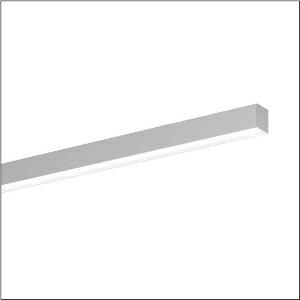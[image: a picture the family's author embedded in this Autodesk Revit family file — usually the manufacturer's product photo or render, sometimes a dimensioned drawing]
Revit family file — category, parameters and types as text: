
# Revit family: silica_r__21_51mx20da42sb_9e9a
name_source: partatom
category: Lighting Fixtures
units: mm (PartAtom-declared; Revit-internal decimal feet)

## family parameters
Cut with Voids When Loaded = No
Host = Face
Light Source = No
Part Type = Normal
Room Calculation Point = No
Round Connector Dimension = Use Diameter
Shared = No

## types (1)
- --- (1 x LED, 2400 lm, 15.2 W, 4000K)
    Apparent Load = 15 VA
    CIE Flux Codes = 48 79 96 100 100
    Color Rendering = 80
    Color Temperature = 4000K
    Default Elevation = 1800 mm
    Description = Silica® 21, office luminaire, primary optical cover: cover, of PMMA, opal, light emission: direct distribution, primary light characteristic: symmetric, installation type: surface-mounted, LED, rated luminous flux: 2.400lm, luminous efficacy: 158lm/W, light colour: 840, colour temperature: 4000K, with terminal, 3+2-pole, max. 2.5mm², mains connection: 220..240V, AC, 50/60Hz, rated input power: 15.2W, luminaire housing, of aluminium, metallic grey (RAL 9006), length: 1.204mm, width: 53mm, height: 53mm, protection rating (complete): IP20, insulation class (complete): insulation class I (protective earthing), certification: CE, permissible operating ambient temperature: 0..+35°C, standard: EN 50419, packaging unit: 1 piece
    Height = 0 mm  [stored 0 ft]
    Lamp = 1 x LED
    Lamp Light Flux = 2400 lm
    Lamp Power = 15.2 W
    Lamp count = 1
    Length = 1204 mm
    Luminous efficacy = 158 lm/W
    Manufacturer = Siteco
    ModVariant = No
    Model = 51MX20DA42SB
    Mounting Place = Ceiling
    Mounting Type = Recessed
    Number of Poles = 1
    OnlyDefault = Yes
    Power Factor = 1
    Product Name = Silica® 21
    Product group = office luminaire | ceiling recessed
    ProductGroupID = 401
    Protection Class = Protection class I
    Protection Degree = IP 20
    RLX_Detail_Level = 1
    RLX_Emergency_Light_Flux = 0 lm
    RLX_Emergency_Type = 0
    RLX_Emergency_Type_DB = No
    RlxData = <blob elided: 26337 chars, md5=e2a91040>
    Socket = socket
    Standby Power = 0 W
    System Light Flux = 2400 lm
    System Power = 15 W
    Type Comments = factory setting: luminous flux: 100 % | dim-lin: 254 | 218 mA
    Type Image = l_1297768.jpg
    URL = http://relux.com
    VarID = @adj_048209
    Voltage = 0 V
    Weight = 0.00 kg
    Width = 53 mm

note: [stored X ft] marks values corroborated as IEEE doubles in the binary element streams (Revit-internal decimal feet)

## geometry (parser evidence)
native form markers: Blend x4, Sweep x9
no freeform markers — native parametric forms only
